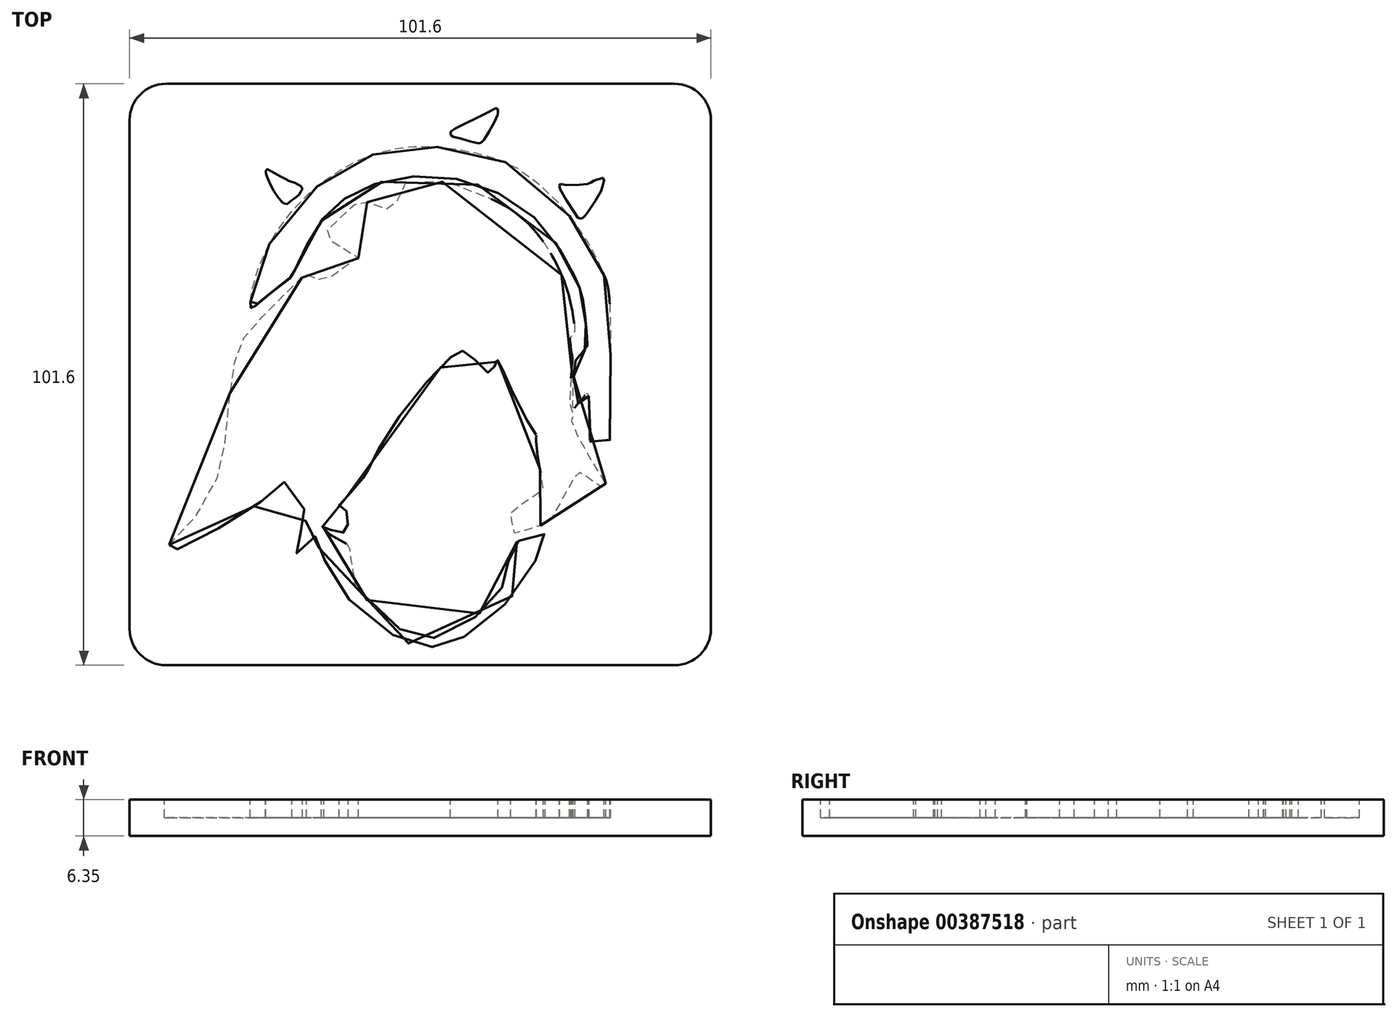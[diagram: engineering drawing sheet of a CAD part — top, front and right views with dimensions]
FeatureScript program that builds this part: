
annotation { "Feature Type Name" : "Feature", "Feature Type Description" : "" }
export const myFeature = defineFeature(function(context is Context, id is Id, definition is map)
    precondition{}
    {
        {
            var Q0;
            Q0=qCreatedBy(makeId("Top.planeOp"),FACE);
            var sketch = newSketch(context, id + "F0", { "sketchPlane" : qUnion([Q0])});
            skLineSegment(sketch, "E0.bottom", {"start": v(-44.45, 50.8) * mm, "end": v(44.45, 50.8) * mm});
            skLineSegment(sketch, "E0.top", {"start": v(-44.45, -50.8) * mm, "end": v(44.45, -50.8) * mm});
            skLineSegment(sketch, "E0.left", {"start": v(-50.8, 44.45) * mm, "end": v(-50.8, -44.45) * mm});
            skLineSegment(sketch, "E0.right", {"start": v(50.8, 44.45) * mm, "end": v(50.8, -44.45) * mm});
            skPoint(sketch, "E1.visualSharp", {"position": v(-50.8, 50.8) * mm});
            skArc(sketch, "E1.filletArc", {"start": v(-44.45, 50.8) * mm, "mid": v(-48.94, 48.94) * mm, "end": v(-50.8, 44.45) * mm});
            skPoint(sketch, "E2.visualSharp", {"position": v(50.8, 50.8) * mm});
            skArc(sketch, "E2.filletArc", {"start": v(50.8, 44.45) * mm, "mid": v(48.94, 48.94) * mm, "end": v(44.45, 50.8) * mm});
            skPoint(sketch, "E3.visualSharp", {"position": v(-50.8, -50.8) * mm});
            skArc(sketch, "E3.filletArc", {"start": v(-50.8, -44.45) * mm, "mid": v(-48.94, -48.94) * mm, "end": v(-44.45, -50.8) * mm});
            skPoint(sketch, "E4.visualSharp", {"position": v(50.8, -50.8) * mm});
            skArc(sketch, "E4.filletArc", {"start": v(44.45, -50.8) * mm, "mid": v(48.94, -48.94) * mm, "end": v(50.8, -44.45) * mm});
            skSolve(sketch);
        }
        {
            var Q0;
            Q0=makeQuery(id+"F0.imprint","IMPRINT",FACE,{"disambiguationData":[TD([[makeQuery(id+"F0.imprint","IMPRINT",EDGE,{"derivedFrom":sQuery(id+"F0.wireOp",EDGE,"E0.bottom")}),-1.0]])]});
            extrude(context, id + "F1", {"entities" : qUnion([Q0]), "depth" : 6.35 * mm});
        }
        {
            var Q0;
            Q0=makeQuery(id+"F1.opExtrude","CAP_FACE",FACE,{"disambiguationData":[OSD([sQuery(id+"F0.wireOp",EDGE,"E0.bottom"),sQuery(id+"F0.wireOp",EDGE,"E0.top"),sQuery(id+"F0.wireOp",EDGE,"E0.left"),sQuery(id+"F0.wireOp",EDGE,"E0.right"),sQuery(id+"F0.wireOp",EDGE,"E1.filletArc"),sQuery(id+"F0.wireOp",EDGE,"E2.filletArc"),sQuery(id+"F0.wireOp",EDGE,"E3.filletArc"),sQuery(id+"F0.wireOp",EDGE,"E4.filletArc")])],"isStart":false});
            var sketch = newSketch(context, id + "F2", { "sketchPlane" : qUnion([Q0])});
            skFitSpline(sketch, "E5", {"points": [v(-29.7, 12.74) * mm, v(-28.45, 18.15) * mm, v(-23.22, 27.6) * mm, v(-15.67, 34.66) * mm, v(-8.65, 38.33) * mm, v(-0.96, 39.86) * mm, v(8.45, 39) * mm, v(17.96, 35.43) * mm, v(28.08, 24.98) * mm, v(32.02, 17.65) * mm, v(33.1, 12.45) * mm, v(33.16, -10.5) * mm, v(33.15, -11.42) * mm, v(33.1, -11.52) * mm, v(32.86, -11.58) * mm, v(31.28, -11.6) * mm, v(30.52, -11.76) * mm, v(29.83, -11.77) * mm, v(29.63, -11.62) * mm, v(29.53, -11.45) * mm, v(29.52, -11.24) * mm, v(29.42, -3.72) * mm, v(29.33, -3.44) * mm, v(29.06, -3.34) * mm, v(28.76, -3.63) * mm, v(28.43, -4.12) * mm, v(27.94, -4.67) * mm, v(27.39, -5.28) * mm, v(26.93, -5.82) * mm, v(26.7, -5.78) * mm, v(26.66, -5.51) * mm, v(26.97, 2.29) * mm, v(27.12, 2.48) * mm, v(27.24, 2.67) * mm, v(27.9, 3.45) * mm, v(29, 4.55) * mm, v(29.17, 4.9) * mm, v(29.27, 5.24) * mm, v(29.24, 5.73) * mm, v(28.92, 9.3) * mm, v(28.55, 12.2) * mm, v(28.02, 14.84) * mm, v(27.72, 15.4) * mm, v(26.94, 17.16) * mm, v(19.67, 27.66) * mm, v(1.65, 34.72) * mm, v(-12.65, 31.1) * mm, v(-18.71, 24.68) * mm, v(-22.33, 17.44) * mm, v(-22.7, 16.9) * mm, v(-23.15, 16.53) * mm, v(-28.43, 12.4) * mm, v(-28.92, 11.95) * mm, v(-29.2, 11.75) * mm, v(-29.46, 11.66) * mm, v(-29.6, 11.66) * mm, v(-29.66, 11.72) * mm, v(-29.7, 11.97) * mm, v(-29.7, 12.74) * mm]});
            skFitSpline(sketch, "E6", {"points": [v(-26.95, 35) * mm, v(-27.04, 35.33) * mm, v(-27.03, 35.54) * mm, v(-27.02, 35.74) * mm, v(-26.76, 35.88) * mm, v(-26.3, 35.62) * mm, v(-25.84, 35.4) * mm, v(-25.25, 35.09) * mm, v(-24.45, 34.64) * mm, v(-23.85, 34.3) * mm, v(-23.3, 34.02) * mm, v(-22.27, 33.58) * mm, v(-21.63, 33.37) * mm, v(-21.33, 33.17) * mm, v(-21.09, 33.07) * mm, v(-20.89, 32.96) * mm, v(-20.76, 32.81) * mm, v(-20.6, 32.5) * mm, v(-20.65, 32.3) * mm, v(-20.74, 32.16) * mm, v(-20.86, 31.96) * mm, v(-20.95, 31.79) * mm, v(-21.52, 31.1) * mm, v(-22.01, 30.74) * mm, v(-22.3, 30.6) * mm, v(-23.06, 29.84) * mm, v(-23.42, 29.8) * mm, v(-23.56, 29.8) * mm, v(-23.77, 29.87) * mm, v(-23.9, 29.94) * mm, v(-24.08, 30.08) * mm, v(-25.04, 31.2) * mm, v(-25.65, 32.19) * mm, v(-26.3, 33.44) * mm, v(-26.7, 34.32) * mm, v(-26.95, 35) * mm]});
            skFitSpline(sketch, "E7", {"points": [v(5.73, 41.57) * mm, v(5.53, 41.6) * mm, v(5.37, 41.81) * mm, v(5.3, 41.93) * mm, v(5.29, 42.25) * mm, v(5.37, 42.48) * mm, v(5.53, 42.6) * mm, v(6, 42.9) * mm, v(12.47, 46.17) * mm, v(12.9, 46.41) * mm, v(13.24, 46.5) * mm, v(13.41, 46.5) * mm, v(13.47, 46.41) * mm, v(13.59, 46.09) * mm, v(13.58, 45.78) * mm, v(13.58, 45.6) * mm, v(13.46, 45.2) * mm, v(10.98, 40.83) * mm, v(10.68, 40.56) * mm, v(10.63, 40.52) * mm, v(10.5, 40.5) * mm, v(10.33, 40.45) * mm, v(10.12, 40.41) * mm, v(5.73, 41.57) * mm]});
            skFitSpline(sketch, "E8", {"points": [v(28.82, 27.78) * mm, v(28.6, 27.51) * mm, v(28.4, 27.4) * mm, v(28.18, 27.3) * mm, v(28.08, 27.26) * mm, v(27.77, 27.24) * mm, v(27.57, 27.35) * mm, v(27.26, 27.8) * mm, v(24.4, 32.46) * mm, v(24.34, 32.81) * mm, v(24.31, 33.02) * mm, v(24.29, 33.15) * mm, v(24.49, 33.27) * mm, v(24.8, 33.2) * mm, v(28.84, 33.24) * mm, v(29.28, 33.35) * mm, v(29.8, 33.53) * mm, v(30.13, 33.73) * mm, v(30.37, 33.9) * mm, v(30.62, 33.97) * mm, v(31.01, 34.1) * mm, v(31.23, 34.17) * mm, v(31.55, 34.28) * mm, v(31.89, 34.4) * mm, v(32.13, 34.12) * mm, v(32.1, 33.84) * mm, v(32.05, 33.58) * mm, v(31.98, 33.37) * mm, v(31.89, 33.02) * mm, v(31.82, 32.75) * mm, v(31.38, 31.59) * mm, v(28.98, 28.01) * mm, v(28.82, 27.78) * mm]});
            skFitSpline(sketch, "E9", {"points": [v(-43.9, -29.75) * mm, v(-37.53, -22.4) * mm, v(-34.4, -13.81) * mm, v(-33.6, -6.58) * mm, v(-32.1, 3.61) * mm, v(-30.84, 6.36) * mm, v(-29.06, 8.54) * mm, v(-21.39, 16.3) * mm, v(-20.64, 17.02) * mm, v(-20.11, 17.52) * mm, v(-19.91, 17.52) * mm, v(-19.67, 17.42) * mm, v(-17.9, 16.64) * mm, v(-16.9, 16.5) * mm, v(-15.87, 16.9) * mm, v(-13.38, 19) * mm, v(-11.44, 19.83) * mm, v(-10.86, 20.22) * mm, v(-10.86, 20.4) * mm, v(-11.43, 20.74) * mm, v(-16.5, 23.95) * mm, v(-16.81, 24.32) * mm, v(-16.52, 24.91) * mm, v(-11.33, 29.88) * mm, v(-10.9, 30.12) * mm, v(-9.57, 30.15) * mm, v(-9.08, 30) * mm, v(-5.95, 29) * mm, v(-5.24, 28.9) * mm, v(-4.54, 29.25) * mm, v(-3.04, 33.01) * mm, v(-2.69, 33.42) * mm, v(-1.97, 33.57) * mm, v(3.95, 33.68) * mm, v(5.96, 33.22) * mm, v(14, 29.9) * mm, v(20.67, 24.31) * mm, v(25.65, 14.84) * mm, v(26.99, 8.16) * mm, v(26.97, 7.58) * mm, v(26.87, 7.33) * mm, v(26.64, 6.97) * mm, v(26.19, 6.37) * mm, v(26.15, 6.27) * mm, v(26.56, 3.03) * mm, v(26.61, 2.58) * mm, v(26.19, -6.03) * mm, v(26.5, -6.4) * mm, v(26.7, -6.8) * mm, v(26.7, -7.36) * mm, v(26.47, -7.76) * mm, v(26.45, -8.45) * mm, v(32.05, -18.49) * mm, v(32.43, -19.15) * mm, v(32.23, -19.71) * mm, v(31.55, -19.6) * mm, v(28.3, -17.31) * mm, v(27.8, -17.1) * mm, v(27.39, -17.38) * mm, v(22.89, -25.31) * mm, v(22.1, -26) * mm, v(16.68, -27.71) * mm, v(16.4, -27.56) * mm, v(15.83, -24.42) * mm, v(16, -23.96) * mm, v(21.14, -20.31) * mm, v(21.48, -19.99) * mm, v(20.73, -15.47) * mm, v(20.25, -11.06) * mm, v(20.27, -10.61) * mm, v(19.83, -9.98) * mm, v(16.05, -2.87) * mm, v(13.96, 1.72) * mm, v(13.62, 2.33) * mm, v(13.44, 2.65) * mm, v(13.22, 2.08) * mm, v(12.28, 0.42) * mm, v(12, 0.27) * mm, v(11.37, 0.78) * mm, v(8.07, 3.8) * mm, v(7.27, 4.12) * mm, v(6.22, 3.7) * mm, v(-3.1, -6.55) * mm, v(-8.9, -16.13) * mm, v(-9.58, -17.58) * mm, v(-10.28, -18.39) * mm, v(-13.8, -22.4) * mm, v(-14.2, -22.8) * mm, v(-13.75, -23.26) * mm, v(-12.89, -23.85) * mm, v(-12.62, -25.65) * mm, v(-12.89, -27.46) * mm, v(-13.64, -27.62) * mm, v(-15.34, -27.3) * mm, v(-16.68, -26.51) * mm, v(-17.06, -26.51) * mm, v(-17.25, -27) * mm, v(-14.37, -28.67) * mm, v(-12.52, -30.12) * mm, v(-12.2, -31.76) * mm, v(-11.56, -35.84) * mm, v(-11.3, -36.97) * mm, v(-5.65, -42.95) * mm, v(-1.19, -45.64) * mm, v(1.59, -46.07) * mm, v(5.27, -45.26) * mm, v(10.73, -41.39) * mm, v(13.5, -38.26) * mm, v(14.66, -36.58) * mm, v(14.9, -35.34) * mm, v(15.38, -32.64) * mm, v(15.64, -30.69) * mm, v(15.76, -30.26) * mm, v(16.37, -29.61) * mm, v(20.71, -27.27) * mm, v(21.34, -27.29) * mm, v(21.59, -27.74) * mm, v(21.81, -28.47) * mm, v(21.26, -29.8) * mm, v(19.78, -33.26) * mm, v(15.48, -39.41) * mm, v(10.33, -44.1) * mm, v(5.53, -47.04) * mm, v(3.67, -47.55) * mm, v(0.24, -47.55) * mm, v(-3.62, -46.24) * mm, v(-10.81, -40.83) * mm, v(-14.05, -37.34) * mm, v(-16.83, -32.22) * mm, v(-17.73, -30.24) * mm, v(-18.27, -28.8) * mm, v(-18.43, -28.06) * mm, v(-18.56, -27.9) * mm, v(-18.94, -28.16) * mm, v(-21.6, -31.23) * mm, v(-22.08, -31.33) * mm, v(-22.37, -31.14) * mm, v(-22.2, -30.37) * mm, v(-20.03, -25.66) * mm, v(-19.9, -25.09) * mm, v(-19.94, -24.54) * mm, v(-20.51, -23.17) * mm, v(-23.24, -19.2) * mm, v(-23.64, -18.82) * mm, v(-23.83, -18.78) * mm, v(-24.15, -19.03) * mm, v(-25.73, -20.66) * mm, v(-30.82, -24.15) * mm, v(-36.12, -27.35) * mm, v(-41.04, -29.93) * mm, v(-44.03, -31) * mm, v(-44.52, -30.95) * mm, v(-44.7, -30.66) * mm, v(-43.9, -29.75) * mm]});
            skSolve(sketch);
        }
        {
            var Q0;
            Q0 = qSketchRegion(id + "F2", true);
            extrude(context, id + "F3", {"entities" : qUnion([Q0]), "operationType" : NewBodyOperationType.REMOVE, "oppositeDirection" : true, "depth" : 3.17 * mm});
        }
    });
